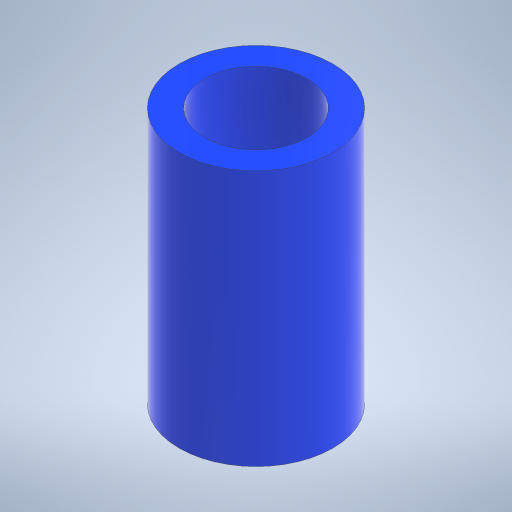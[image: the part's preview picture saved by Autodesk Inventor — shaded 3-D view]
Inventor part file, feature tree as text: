
AUTODESK INVENTOR PART (.ipt)
format: ipt  version: 2024.3 (Build 283343000, 343)  size: 217,088 bytes
history: native  units: mm
features: extrude x1, sketch x1
ambient origin geometry x8: Origin, YZ Plane, XZ Plane, XY Plane, X Axis, Y Axis, Z Axis, Center Point
bodies: Solid1 (feature_tree)
feature tree (2):
  extrude  "Extrusion1"  Depth=5.0mm
  sketch  "Sketch1"  dims[d0=3.0mm d1=2.0mm d2=5.0mm d3=0.0mm]
